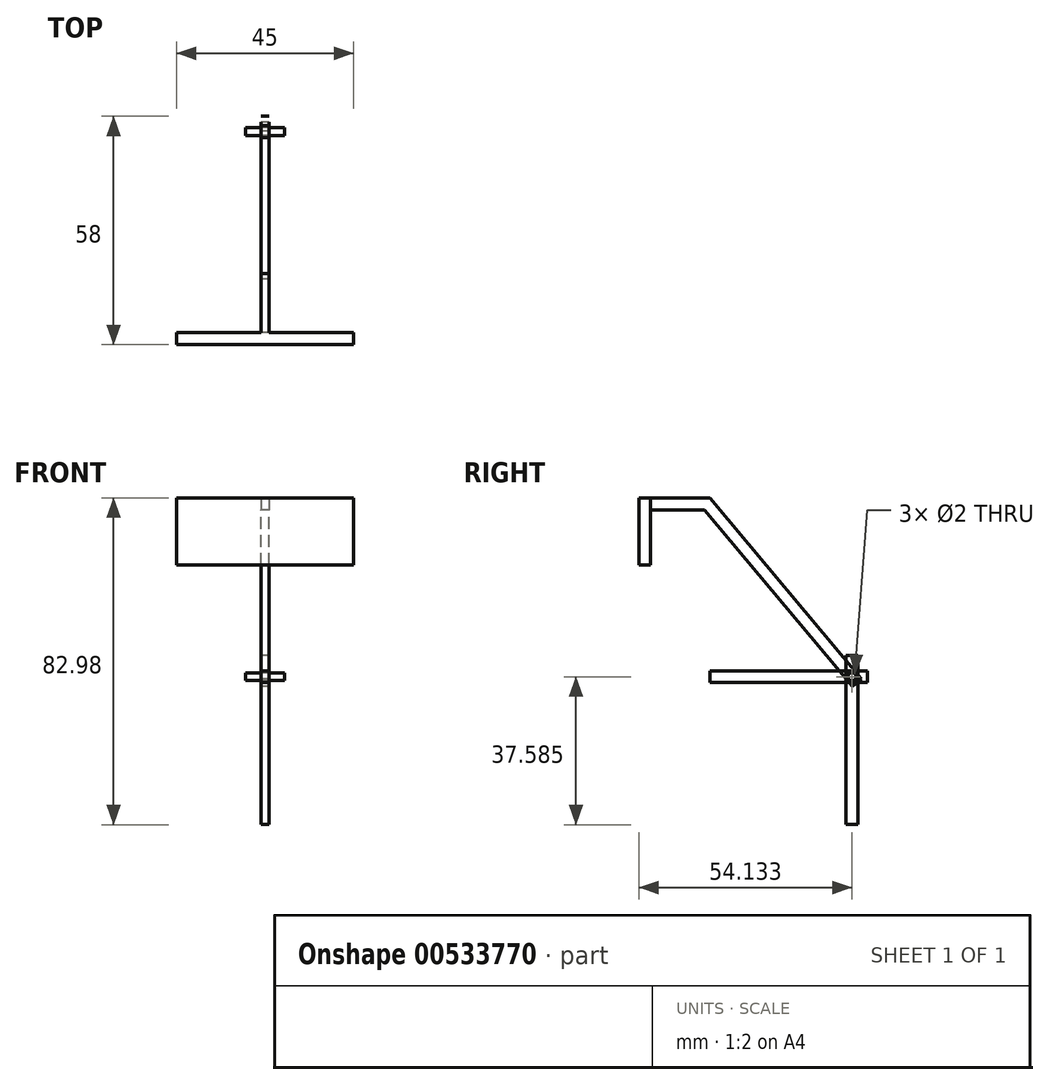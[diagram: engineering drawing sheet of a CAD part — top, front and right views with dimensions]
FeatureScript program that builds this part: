
annotation { "Feature Type Name" : "Feature", "Feature Type Description" : "" }
export const myFeature = defineFeature(function(context is Context, id is Id, definition is map)
    precondition{}
    {
        {
            var Q0;
            Q0=qCreatedBy(makeId("Right.planeOp"),FACE);
            var sketch = newSketch(context, id + "F0", { "sketchPlane" : qUnion([Q0])});
            skLineSegment(sketch, "E0.bottom", {"start": v(-1.5, 8.5) * mm, "end": v(1.5, 8.5) * mm});
            skLineSegment(sketch, "E0.top", {"start": v(-1.5, -8.5) * mm, "end": v(1.5, -8.5) * mm});
            skLineSegment(sketch, "E0.left", {"start": v(-1.5, 8.5) * mm, "end": v(-1.5, -8.5) * mm});
            skLineSegment(sketch, "E0.right", {"start": v(1.5, 8.5) * mm, "end": v(1.5, -8.5) * mm});
            skPoint(sketch, "E0.middle", {"position": v(0, 0) * mm});
            skLineSegment(sketch, "E1.bottom", {"start": v(1.5, 8.5) * mm, "end": v(16.5, 8.5) * mm});
            skLineSegment(sketch, "E1.top", {"start": v(1.5, 5.5) * mm, "end": v(16.5, 5.5) * mm});
            skLineSegment(sketch, "E1.left", {"start": v(1.5, 8.5) * mm, "end": v(1.5, 5.5) * mm});
            skLineSegment(sketch, "E1.right", {"start": v(16.5, 8.5) * mm, "end": v(16.5, 5.5) * mm});
            skLineSegment(sketch, "E2", {"start": v(16.5, 8.5) * mm, "end": v(55.07, -37.46) * mm});
            skLineSegment(sketch, "E3", {"start": v(55.07, -37.46) * mm, "end": v(52.77, -39.4) * mm});
            skLineSegment(sketch, "E4", {"start": v(52.77, -39.4) * mm, "end": v(15.1, 5.5) * mm});
            skCircle(sketch, "E5", {"center": v(52.63, -36.9) * mm, "radius": 1 * mm});
            skLineSegment(sketch, "E6", {"start": v(51.48, -37.86) * mm, "end": v(53.78, -35.93) * mm, "construction": true});
            skLineSegment(sketch, "E7", {"start": v(52.63, -36.9) * mm, "end": v(16.5, -36.9) * mm, "construction": true});
            skLineSegment(sketch, "E8", {"start": v(16.5, -35.4) * mm, "end": v(16.5, -38.4) * mm});
            skLineSegment(sketch, "E9", {"start": v(16.5, -35.4) * mm, "end": v(56.5, -35.4) * mm});
            skLineSegment(sketch, "E10", {"start": v(56.5, -35.4) * mm, "end": v(56.5, -38.4) * mm});
            skLineSegment(sketch, "E11", {"start": v(56.5, -38.4) * mm, "end": v(16.5, -38.4) * mm});
            skLineSegment(sketch, "E12", {"start": v(52.63, -36.9) * mm, "end": v(52.63, -74.48) * mm, "construction": true});
            skLineSegment(sketch, "E13", {"start": v(51.13, -74.48) * mm, "end": v(54.13, -74.48) * mm});
            skLineSegment(sketch, "E14", {"start": v(51.13, -74.48) * mm, "end": v(51.13, -31.48) * mm});
            skLineSegment(sketch, "E15", {"start": v(51.13, -31.48) * mm, "end": v(54.13, -31.48) * mm});
            skLineSegment(sketch, "E16", {"start": v(54.13, -31.48) * mm, "end": v(54.13, -74.48) * mm});
            skSolve(sketch);
        }
        {
            var Q0;
            {var subQ1=sQuery(id+"F0.wireOp",EDGE,"E8");Q0=makeQuery(id+"F0.imprint","IMPRINT",FACE,{"disambiguationData":[TD([[makeQuery(id+"F0.imprint","IMPRINT",EDGE,{"derivedFrom":subQ1}),1.0]])]});}
            var Q1;
            {var subQ0=sQuery(id+"F0.wireOp",EDGE,"E9");var subQ1=sQuery(id+"F0.wireOp",EDGE,"E4");var subQ2=makeQuery(id+"F0.imprint","INTERSECT",VERTEX,{"derivedFrom":[subQ1,subQ0]});Q1=makeQuery(id+"F0.imprint","IMPRINT",FACE,{"disambiguationData":[TD([[makeQuery(id+"F0.imprint","IMPRINT",EDGE,{"disambiguationData":[TD([[subQ2,1.0]])],"derivedFrom":subQ1}),-1.0]])]});}
            var Q2;
            Q2=makeQuery(id+"F0.imprint","IMPRINT",FACE,{"disambiguationData":[TD([[makeQuery(id+"F0.imprint","IMPRINT",EDGE,{"derivedFrom":sQuery(id+"F0.wireOp",EDGE,"E5")}),-1.0]])]});
            var Q3;
            {var subQ0=sQuery(id+"F0.wireOp",EDGE,"E11");var subQ1=sQuery(id+"F0.wireOp",EDGE,"E4");var subQ2=makeQuery(id+"F0.imprint","INTERSECT",VERTEX,{"derivedFrom":[subQ1,subQ0]});Q3=makeQuery(id+"F0.imprint","IMPRINT",FACE,{"disambiguationData":[TD([[makeQuery(id+"F0.imprint","IMPRINT",EDGE,{"disambiguationData":[TD([[subQ2,-1.0]])],"derivedFrom":subQ1}),1.0]])]});}
            var Q4;
            {var subQ0=sQuery(id+"F0.wireOp",EDGE,"E9");var subQ1=sQuery(id+"F0.wireOp",EDGE,"E2");var subQ2=makeQuery(id+"F0.imprint","INTERSECT",VERTEX,{"derivedFrom":[subQ1,subQ0]});Q4=makeQuery(id+"F0.imprint","IMPRINT",FACE,{"disambiguationData":[TD([[makeQuery(id+"F0.imprint","IMPRINT",EDGE,{"disambiguationData":[TD([[subQ2,-1.0]])],"derivedFrom":subQ1}),1.0]])]});}
            var Q5;
            {var subQ0=sQuery(id+"F0.wireOp",EDGE,"E10");Q5=makeQuery(id+"F0.imprint","IMPRINT",FACE,{"disambiguationData":[TD([[makeQuery(id+"F0.imprint","IMPRINT",EDGE,{"derivedFrom":subQ0}),-1.0]])]});}
            var Q6;
            {var subQ0=sQuery(id+"F0.wireOp",EDGE,"E3");var subQ1=sQuery(id+"F0.wireOp",EDGE,"E2");var subQ2=makeQuery(id+"F0.imprint","INTERSECT",VERTEX,{"derivedFrom":[subQ1,subQ0]});Q6=makeQuery(id+"F0.imprint","IMPRINT",FACE,{"disambiguationData":[TD([[makeQuery(id+"F0.imprint","IMPRINT",EDGE,{"disambiguationData":[TD([[subQ2,1.0]])],"derivedFrom":subQ1}),-1.0]])]});}
            var Q7;
            {var subQ0=sQuery(id+"F0.wireOp",EDGE,"E16");var subQ1=sQuery(id+"F0.wireOp",EDGE,"E3");var subQ2=makeQuery(id+"F0.imprint","INTERSECT",VERTEX,{"derivedFrom":[subQ1,subQ0]});Q7=makeQuery(id+"F0.imprint","IMPRINT",FACE,{"disambiguationData":[TD([[makeQuery(id+"F0.imprint","IMPRINT",EDGE,{"disambiguationData":[TD([[subQ2,-1.0]])],"derivedFrom":subQ1}),1.0]])]});}
            extrude(context, id + "F1", {"entities" : qUnion([Q0, Q1, Q2, Q3, Q4, Q5, Q6, Q7]), "endBound" : BoundingType.SYMMETRIC, "depth" : 2 * mm, "offsetDistance" : 25 * mm});
        }
        {
            var Q0;
            {var subQ0=sQuery(id+"F0.wireOp",EDGE,"E15");Q0=makeQuery(id+"F0.imprint","IMPRINT",FACE,{"disambiguationData":[TD([[makeQuery(id+"F0.imprint","IMPRINT",EDGE,{"derivedFrom":subQ0}),-1.0]])]});}
            var Q1;
            {var subQ0=sQuery(id+"F0.wireOp",EDGE,"E14");var subQ1=sQuery(id+"F0.wireOp",EDGE,"E2");var subQ2=makeQuery(id+"F0.imprint","INTERSECT",VERTEX,{"derivedFrom":[subQ1,subQ0]});Q1=makeQuery(id+"F0.imprint","IMPRINT",FACE,{"disambiguationData":[TD([[makeQuery(id+"F0.imprint","IMPRINT",EDGE,{"disambiguationData":[TD([[subQ2,-1.0]])],"derivedFrom":subQ1}),-1.0]])]});}
            var Q2;
            Q2=makeQuery(id+"F0.imprint","IMPRINT",FACE,{"disambiguationData":[TD([[makeQuery(id+"F0.imprint","IMPRINT",EDGE,{"derivedFrom":sQuery(id+"F0.wireOp",EDGE,"E5")}),-1.0]])]});
            var Q3;
            {var subQ0=sQuery(id+"F0.wireOp",EDGE,"E11");var subQ1=sQuery(id+"F0.wireOp",EDGE,"E4");var subQ2=makeQuery(id+"F0.imprint","INTERSECT",VERTEX,{"derivedFrom":[subQ1,subQ0]});Q3=makeQuery(id+"F0.imprint","IMPRINT",FACE,{"disambiguationData":[TD([[makeQuery(id+"F0.imprint","IMPRINT",EDGE,{"disambiguationData":[TD([[subQ2,-1.0]])],"derivedFrom":subQ1}),1.0]])]});}
            var Q4;
            {var subQ0=sQuery(id+"F0.wireOp",EDGE,"E9");var subQ1=sQuery(id+"F0.wireOp",EDGE,"E2");var subQ2=makeQuery(id+"F0.imprint","INTERSECT",VERTEX,{"derivedFrom":[subQ1,subQ0]});Q4=makeQuery(id+"F0.imprint","IMPRINT",FACE,{"disambiguationData":[TD([[makeQuery(id+"F0.imprint","IMPRINT",EDGE,{"disambiguationData":[TD([[subQ2,-1.0]])],"derivedFrom":subQ1}),1.0]])]});}
            var Q5;
            {var subQ10=sQuery(id+"F0.wireOp",EDGE,"E13");Q5=makeQuery(id+"F0.imprint","IMPRINT",FACE,{"disambiguationData":[TD([[makeQuery(id+"F0.imprint","IMPRINT",EDGE,{"derivedFrom":subQ10}),1.0]])]});}
            var Q6;
            {var subQ0=sQuery(id+"F0.wireOp",EDGE,"E4");var subQ1=sQuery(id+"F0.wireOp",EDGE,"E3");var subQ2=makeQuery(id+"F0.imprint","INTERSECT",VERTEX,{"derivedFrom":[subQ1,subQ0]});Q6=makeQuery(id+"F0.imprint","IMPRINT",FACE,{"disambiguationData":[TD([[makeQuery(id+"F0.imprint","IMPRINT",EDGE,{"disambiguationData":[TD([[subQ2,1.0]])],"derivedFrom":subQ1}),-1.0]])]});}
            var Q7;
            {var subQ0=sQuery(id+"F0.wireOp",EDGE,"E16");var subQ1=sQuery(id+"F0.wireOp",EDGE,"E3");var subQ2=makeQuery(id+"F0.imprint","INTERSECT",VERTEX,{"derivedFrom":[subQ1,subQ0]});Q7=makeQuery(id+"F0.imprint","IMPRINT",FACE,{"disambiguationData":[TD([[makeQuery(id+"F0.imprint","IMPRINT",EDGE,{"disambiguationData":[TD([[subQ2,-1.0]])],"derivedFrom":subQ1}),1.0]])]});}
            extrude(context, id + "F2", {"entities" : qUnion([Q0, Q1, Q2, Q3, Q4, Q5, Q6, Q7]), "endBound" : BoundingType.SYMMETRIC, "depth" : 2 * mm, "offsetDistance" : 25 * mm});
        }
        {
            var Q0;
            {var subQ0=sQuery(id+"F0.wireOp",EDGE,"E3");var subQ1=sQuery(id+"F0.wireOp",EDGE,"E2");var subQ2=makeQuery(id+"F0.imprint","INTERSECT",VERTEX,{"derivedFrom":[subQ1,subQ0]});Q0=makeQuery(id+"F0.imprint","IMPRINT",FACE,{"disambiguationData":[TD([[makeQuery(id+"F0.imprint","IMPRINT",EDGE,{"disambiguationData":[TD([[subQ2,1.0]])],"derivedFrom":subQ1}),-1.0]])]});}
            var Q1;
            {var subQ0=sQuery(id+"F0.wireOp",EDGE,"E4");var subQ1=sQuery(id+"F0.wireOp",EDGE,"E3");var subQ2=makeQuery(id+"F0.imprint","INTERSECT",VERTEX,{"derivedFrom":[subQ1,subQ0]});Q1=makeQuery(id+"F0.imprint","IMPRINT",FACE,{"disambiguationData":[TD([[makeQuery(id+"F0.imprint","IMPRINT",EDGE,{"disambiguationData":[TD([[subQ2,1.0]])],"derivedFrom":subQ1}),-1.0]])]});}
            var Q2;
            Q2=makeQuery(id+"F0.imprint","IMPRINT",FACE,{"disambiguationData":[TD([[makeQuery(id+"F0.imprint","IMPRINT",EDGE,{"derivedFrom":sQuery(id+"F0.wireOp",EDGE,"E5")}),-1.0]])]});
            var Q3;
            {var subQ0=sQuery(id+"F0.wireOp",EDGE,"E14");var subQ1=sQuery(id+"F0.wireOp",EDGE,"E2");var subQ2=makeQuery(id+"F0.imprint","INTERSECT",VERTEX,{"derivedFrom":[subQ1,subQ0]});Q3=makeQuery(id+"F0.imprint","IMPRINT",FACE,{"disambiguationData":[TD([[makeQuery(id+"F0.imprint","IMPRINT",EDGE,{"disambiguationData":[TD([[subQ2,-1.0]])],"derivedFrom":subQ1}),-1.0]])]});}
            var Q4;
            {var subQ0=sQuery(id+"F0.wireOp",EDGE,"E9");var subQ1=sQuery(id+"F0.wireOp",EDGE,"E4");var subQ2=makeQuery(id+"F0.imprint","INTERSECT",VERTEX,{"derivedFrom":[subQ1,subQ0]});Q4=makeQuery(id+"F0.imprint","IMPRINT",FACE,{"disambiguationData":[TD([[makeQuery(id+"F0.imprint","IMPRINT",EDGE,{"disambiguationData":[TD([[subQ2,1.0]])],"derivedFrom":subQ1}),-1.0]])]});}
            var Q5;
            {var subQ5=sQuery(id+"F0.wireOp",EDGE,"E1.right");Q5=makeQuery(id+"F0.imprint","IMPRINT",FACE,{"disambiguationData":[TD([[makeQuery(id+"F0.imprint","IMPRINT",EDGE,{"derivedFrom":subQ5}),1.0]])]});}
            var Q6;
            Q6=makeQuery(id+"F0.imprint","IMPRINT",FACE,{"disambiguationData":[TD([[makeQuery(id+"F0.imprint","IMPRINT",EDGE,{"derivedFrom":sQuery(id+"F0.wireOp",EDGE,"E1.bottom")}),-1.0]])]});
            extrude(context, id + "F3", {"entities" : qUnion([Q0, Q1, Q2, Q3, Q4, Q5, Q6]), "endBound" : BoundingType.SYMMETRIC, "depth" : 2 * mm, "offsetDistance" : 25 * mm});
        }
        {
            var Q0;
            Q0=makeQuery(id+"F0.imprint","IMPRINT",FACE,{"disambiguationData":[TD([[makeQuery(id+"F0.imprint","IMPRINT",EDGE,{"derivedFrom":sQuery(id+"F0.wireOp",EDGE,"E0.bottom")}),-1.0]])]});
            extrude(context, id + "F4", {"entities" : qUnion([Q0]), "operationType" : NewBodyOperationType.ADD, "endBound" : BoundingType.SYMMETRIC, "depth" : 45 * mm, "offsetDistance" : 25 * mm});
        }
        {
            var Q0;
            Q0=makeQuery(id+"F0.imprint","IMPRINT",FACE,{"disambiguationData":[TD([[makeQuery(id+"F0.imprint","IMPRINT",EDGE,{"derivedFrom":sQuery(id+"F0.wireOp",EDGE,"E5")}),1.0]])]});
            extrude(context, id + "F5", {"entities" : qUnion([Q0]), "endBound" : BoundingType.SYMMETRIC, "depth" : 10 * mm, "offsetDistance" : 25 * mm});
        }
    });
